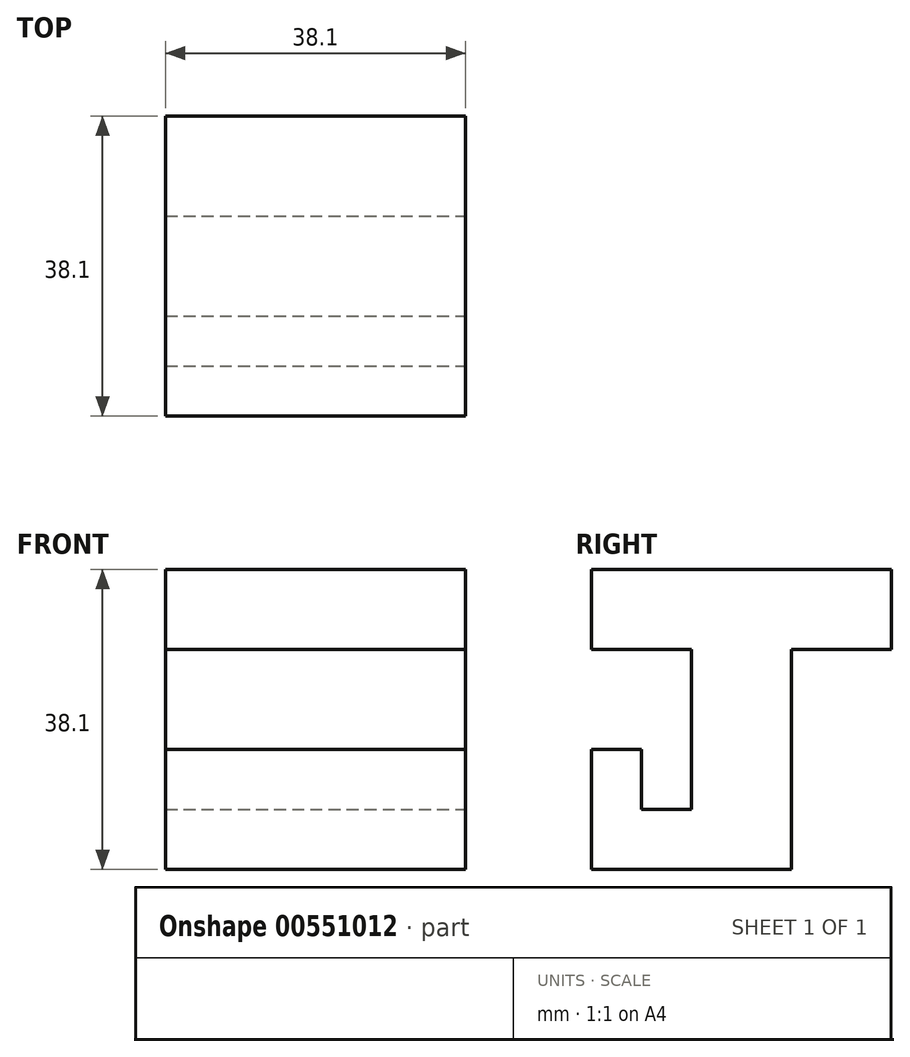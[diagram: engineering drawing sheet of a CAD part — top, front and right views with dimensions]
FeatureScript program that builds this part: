
annotation { "Feature Type Name" : "Feature", "Feature Type Description" : "" }
export const myFeature = defineFeature(function(context is Context, id is Id, definition is map)
    precondition{}
    {
        {
            var Q0;
            Q0=qCreatedBy(makeId("Front.planeOp"),FACE);
            var sketch = newSketch(context, id + "F0", { "sketchPlane" : qUnion([Q0])});
            skLineSegment(sketch, "E0", {"start": v(0, 0) * mm, "end": v(0, 38.1) * mm});
            skLineSegment(sketch, "E1", {"start": v(0, 38.1) * mm, "end": v(38.1, 38.1) * mm});
            skLineSegment(sketch, "E2", {"start": v(38.1, 38.1) * mm, "end": v(38.1, 0) * mm});
            skLineSegment(sketch, "E3", {"start": v(38.1, 0) * mm, "end": v(0, 0) * mm});
            skSolve(sketch);
        }
        {
            var Q0;
            Q0 = qSketchRegion(id + "F0", true);
            extrude(context, id + "F1", {"entities" : qUnion([Q0]), "depth" : 38.1 * mm, "offsetDistance" : 25.4 * mm});
        }
        {
            var Q0;
            Q0=qCreatedBy(makeId("Front.planeOp"),FACE);
            cPlane(context, id + "F2", {"entities" : qUnion([Q0]), "cplaneType" : CPlaneType.OFFSET, "offset" : 38.1 * mm, "width" : 152.4 * mm, "height" : 152.4 * mm});
        }
        {
            var Q0;
            Q0=qCreatedBy(makeId("Right.planeOp"),FACE);
            cPlane(context, id + "F3", {"entities" : qUnion([Q0]), "cplaneType" : CPlaneType.OFFSET, "offset" : 38.1 * mm, "width" : 152.4 * mm, "height" : 152.4 * mm});
        }
        {
            var Q0;
            Q0=qCreatedBy(id+"F3.planeOp",FACE);
            var sketch = newSketch(context, id + "F4", { "sketchPlane" : qUnion([Q0])});
            skLineSegment(sketch, "E4", {"start": v(0, 0) * mm, "end": v(0, 38.1) * mm});
            skLineSegment(sketch, "E5", {"start": v(-38.1, 38.1) * mm, "end": v(-38.1, 0) * mm});
            skLineSegment(sketch, "E6", {"start": v(-38.1, 0) * mm, "end": v(0, 0) * mm});
            skLineSegment(sketch, "E7", {"start": v(-38.1, 38.1) * mm, "end": v(-38.1, 27.94) * mm});
            skLineSegment(sketch, "E8", {"start": v(0, 38.1) * mm, "end": v(0, 27.94) * mm});
            skLineSegment(sketch, "E9", {"start": v(0, 27.94) * mm, "end": v(-12.7, 27.94) * mm});
            skLineSegment(sketch, "E10", {"start": v(-12.7, 27.94) * mm, "end": v(-12.7, 0) * mm});
            skLineSegment(sketch, "E11", {"start": v(-12.7, 0) * mm, "end": v(-38.1, 0) * mm});
            skLineSegment(sketch, "E12", {"start": v(-38.1, 15.24) * mm, "end": v(-31.75, 15.24) * mm});
            skLineSegment(sketch, "E13", {"start": v(-31.75, 15.24) * mm, "end": v(-31.75, 7.62) * mm});
            skLineSegment(sketch, "E14", {"start": v(-31.75, 7.62) * mm, "end": v(-25.4, 7.62) * mm});
            skLineSegment(sketch, "E15", {"start": v(-25.4, 7.62) * mm, "end": v(-25.4, 27.94) * mm});
            skLineSegment(sketch, "E16", {"start": v(-25.4, 27.94) * mm, "end": v(-38.1, 27.94) * mm});
            skSolve(sketch);
        }
        {
            var Q0;
            {var subQ0=sQuery(id+"F4.wireOp",EDGE,"E12");Q0=makeQuery(id+"F4.imprint","IMPRINT",FACE,{"disambiguationData":[TD([[makeQuery(id+"F4.imprint","IMPRINT",EDGE,{"derivedFrom":subQ0}),1.0]])]});}
            var Q1;
            Q1=makeQuery(id+"F4.imprint","IMPRINT",FACE,{"disambiguationData":[TD([[makeQuery(id+"F4.imprint","IMPRINT",EDGE,{"derivedFrom":sQuery(id+"F4.wireOp",EDGE,"E4")}),1.0]])]});
            extrude(context, id + "F5", {"entities" : qUnion([Q0, Q1]), "operationType" : NewBodyOperationType.REMOVE, "oppositeDirection" : true, "depth" : 38.1 * mm, "offsetDistance" : 25.4 * mm});
        }
    });
